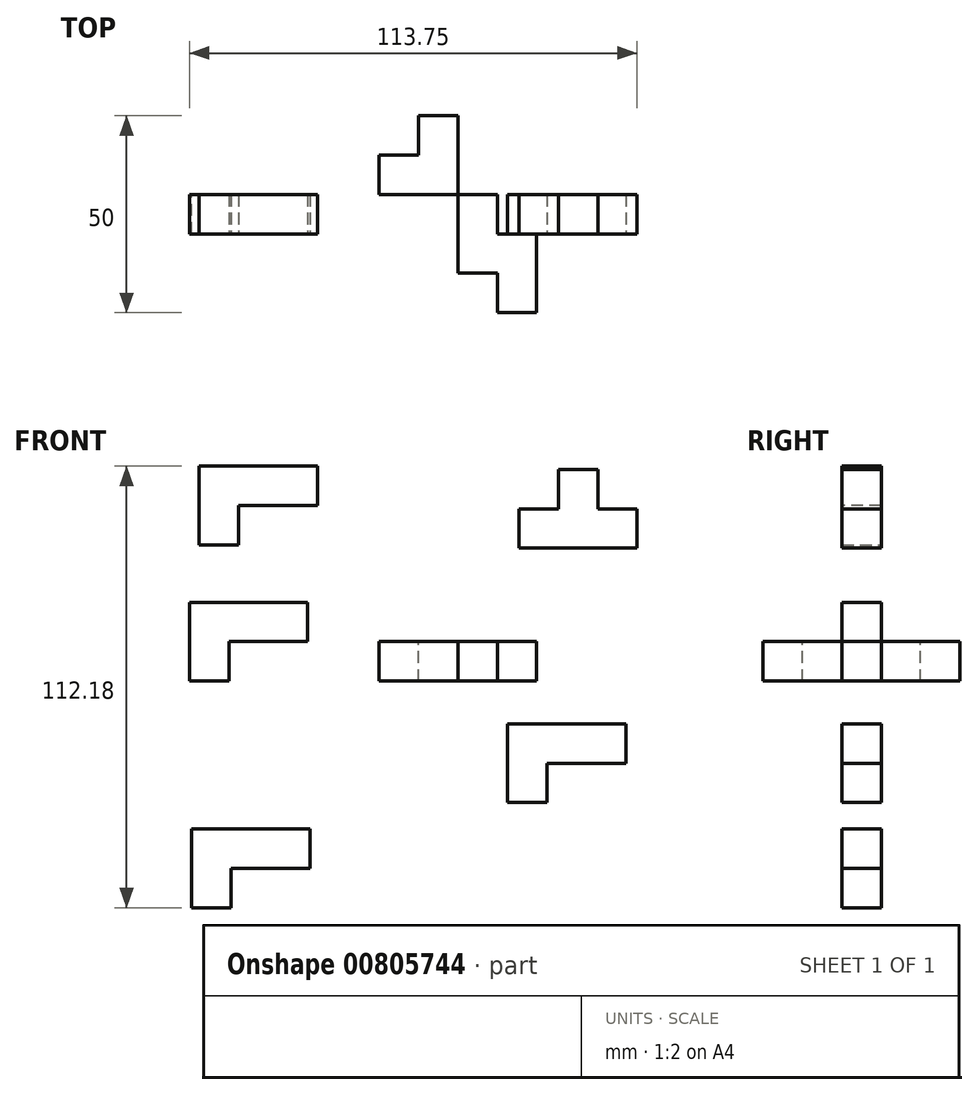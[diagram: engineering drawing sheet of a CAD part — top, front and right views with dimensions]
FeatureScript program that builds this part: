
annotation { "Feature Type Name" : "Feature", "Feature Type Description" : "" }
export const myFeature = defineFeature(function(context is Context, id is Id, definition is map)
    precondition{}
    {
        {
            var Q0;
            Q0=qCreatedBy(makeId("Top.planeOp"),FACE);
            var sketch = newSketch(context, id + "F0", { "sketchPlane" : qUnion([Q0])});
            skLineSegment(sketch, "E0.bottom", {"start": v(0, 0) * mm, "end": v(20, 0) * mm});
            skLineSegment(sketch, "E0.top", {"start": v(0, -30) * mm, "end": v(20, -30) * mm});
            skLineSegment(sketch, "E0.left", {"start": v(0, 0) * mm, "end": v(0, -30) * mm});
            skLineSegment(sketch, "E0.right", {"start": v(20, 0) * mm, "end": v(20, -30) * mm});
            skSolve(sketch);
        }
        {
            var Q0;
            Q0 = qSketchRegion(id + "F0", true);
            extrude(context, id + "F1", {"entities" : qUnion([Q0]), "depth" : 10 * mm, "offsetDistance" : 25 * mm});
        }
        {
            var Q0;
            Q0=makeQuery(id+"F1.opExtrude","CAP_FACE",FACE,{"disambiguationData":[OSD([sQuery(id+"F0.wireOp",EDGE,"E0.bottom"),sQuery(id+"F0.wireOp",EDGE,"E0.top"),sQuery(id+"F0.wireOp",EDGE,"E0.left"),sQuery(id+"F0.wireOp",EDGE,"E0.right")])],"isStart":false});
            var sketch = newSketch(context, id + "F2", { "sketchPlane" : qUnion([Q0])});
            skLineSegment(sketch, "E1.bottom", {"start": v(20, 0) * mm, "end": v(10, 0) * mm});
            skLineSegment(sketch, "E1.top", {"start": v(20, -10) * mm, "end": v(10, -10) * mm});
            skLineSegment(sketch, "E1.left", {"start": v(20, 0) * mm, "end": v(20, -10) * mm});
            skLineSegment(sketch, "E1.right", {"start": v(10, 0) * mm, "end": v(10, -10) * mm});
            skLineSegment(sketch, "E2.bottom", {"start": v(0, -30) * mm, "end": v(10, -30) * mm});
            skLineSegment(sketch, "E2.top", {"start": v(0, -20) * mm, "end": v(10, -20) * mm});
            skLineSegment(sketch, "E2.left", {"start": v(0, -30) * mm, "end": v(0, -20) * mm});
            skLineSegment(sketch, "E2.right", {"start": v(10, -30) * mm, "end": v(10, -20) * mm});
            skSolve(sketch);
        }
        {
            var Q0;
            Q0=qCreatedBy(makeId("Top.planeOp"),FACE);
            var sketch = newSketch(context, id + "F3", { "sketchPlane" : qUnion([Q0])});
            skLineSegment(sketch, "E3.bottom", {"start": v(0, 0) * mm, "end": v(-20, 0) * mm});
            skLineSegment(sketch, "E3.top", {"start": v(0, 20) * mm, "end": v(-20, 20) * mm});
            skLineSegment(sketch, "E3.left", {"start": v(0, 0) * mm, "end": v(0, 20) * mm});
            skLineSegment(sketch, "E3.right", {"start": v(-20, 0) * mm, "end": v(-20, 20) * mm});
            skSolve(sketch);
        }
        {
            var Q0;
            Q0=makeQuery(id+"F3.imprint","IMPRINT",FACE,{"disambiguationData":[TD([[makeQuery(id+"F3.imprint","IMPRINT",EDGE,{"derivedFrom":sQuery(id+"F3.wireOp",EDGE,"E3.bottom")}),-1.0]])]});
            extrude(context, id + "F4", {"entities" : qUnion([Q0]), "depth" : 10 * mm, "offsetDistance" : 25 * mm});
        }
        {
            var Q0;
            Q0=makeQuery(id+"F4.opExtrude","CAP_FACE",FACE,{"disambiguationData":[OSD([sQuery(id+"F3.wireOp",EDGE,"E3.bottom"),sQuery(id+"F3.wireOp",EDGE,"E3.top"),sQuery(id+"F3.wireOp",EDGE,"E3.left"),sQuery(id+"F3.wireOp",EDGE,"E3.right")])],"isStart":false});
            var sketch = newSketch(context, id + "F5", { "sketchPlane" : qUnion([Q0])});
            skSolve(sketch);
        }
        {
            var Q0;
            Q0=makeQuery(id+"F5.imprint","IMPRINT",FACE,{"disambiguationData":[TD([[makeQuery(id+"F5.imprint","IMPRINT",EDGE,{"derivedFrom":makeQuery(id+"F4.opExtrude","CAP_EDGE",EDGE,{"disambiguationData":[OSD([sQuery(id+"F3.wireOp",EDGE,"E3.bottom")])],"isStart":false})}),-1.0]])]});
            var sketch = newSketch(context, id + "F6", { "sketchPlane" : qUnion([Q0])});
            skLineSegment(sketch, "E4.bottom", {"start": v(-20, 20) * mm, "end": v(-10, 20) * mm});
            skLineSegment(sketch, "E4.top", {"start": v(-20, 10) * mm, "end": v(-10, 10) * mm});
            skLineSegment(sketch, "E4.left", {"start": v(-20, 20) * mm, "end": v(-20, 10) * mm});
            skLineSegment(sketch, "E4.right", {"start": v(-10, 20) * mm, "end": v(-10, 10) * mm});
            skSolve(sketch);
        }
        {
            var Q0;
            Q0=makeQuery(id+"F6.imprint","IMPRINT",FACE,{"disambiguationData":[TD([[makeQuery(id+"F6.imprint","IMPRINT",EDGE,{"derivedFrom":sQuery(id+"F6.wireOp",EDGE,"E4.bottom")}),1.0]])]});
            extrude(context, id + "F7", {"entities" : qUnion([Q0]), "operationType" : NewBodyOperationType.REMOVE, "oppositeDirection" : true, "depth" : 10 * mm, "offsetDistance" : 25 * mm});
        }
        {
            var Q0;
            Q0=makeQuery(id+"F2.imprint","IMPRINT",FACE,{"disambiguationData":[TD([[makeQuery(id+"F2.imprint","IMPRINT",EDGE,{"derivedFrom":sQuery(id+"F2.wireOp",EDGE,"E1.bottom")}),-1.0]])]});
            var Q1;
            Q1=makeQuery(id+"F2.imprint","IMPRINT",FACE,{"disambiguationData":[TD([[makeQuery(id+"F2.imprint","IMPRINT",EDGE,{"derivedFrom":sQuery(id+"F2.wireOp",EDGE,"E2.bottom")}),1.0]])]});
            extrude(context, id + "F8", {"entities" : qUnion([Q0, Q1]), "operationType" : NewBodyOperationType.REMOVE, "oppositeDirection" : true, "depth" : 10 * mm, "offsetDistance" : 25 * mm});
        }
        {
            var Q0;
            Q0=qCreatedBy(makeId("Front.planeOp"),FACE);
            var sketch = newSketch(context, id + "F9", { "sketchPlane" : qUnion([Q0])});
            skLineSegment(sketch, "E5.bottom", {"start": v(-68.2, 0) * mm, "end": v(-38.2, 0) * mm});
            skLineSegment(sketch, "E5.top", {"start": v(-68.2, 20) * mm, "end": v(-38.2, 20) * mm});
            skLineSegment(sketch, "E5.left", {"start": v(-68.2, 0) * mm, "end": v(-68.2, 20) * mm});
            skLineSegment(sketch, "E5.right", {"start": v(-38.2, 0) * mm, "end": v(-38.2, 20) * mm});
            skSolve(sketch);
        }
        {
            var Q0;
            Q0=makeQuery(id+"F9.imprint","IMPRINT",FACE,{"disambiguationData":[TD([[makeQuery(id+"F9.imprint","IMPRINT",EDGE,{"derivedFrom":sQuery(id+"F9.wireOp",EDGE,"E5.bottom")}),1.0]])]});
            extrude(context, id + "F10", {"entities" : qUnion([Q0]), "depth" : 10 * mm, "offsetDistance" : 25 * mm});
        }
        {
            var Q0;
            Q0=makeQuery(id+"F10.opExtrude","CAP_FACE",FACE,{"disambiguationData":[OSD([sQuery(id+"F9.wireOp",EDGE,"E5.bottom"),sQuery(id+"F9.wireOp",EDGE,"E5.top"),sQuery(id+"F9.wireOp",EDGE,"E5.left"),sQuery(id+"F9.wireOp",EDGE,"E5.right")])],"isStart":false});
            var sketch = newSketch(context, id + "F11", { "sketchPlane" : qUnion([Q0])});
            skLineSegment(sketch, "E6.bottom", {"start": v(-38.2, 0) * mm, "end": v(-58.2, 0) * mm});
            skLineSegment(sketch, "E6.top", {"start": v(-38.2, 10) * mm, "end": v(-58.2, 10) * mm});
            skLineSegment(sketch, "E6.left", {"start": v(-38.2, 0) * mm, "end": v(-38.2, 10) * mm});
            skLineSegment(sketch, "E6.right", {"start": v(-58.2, 0) * mm, "end": v(-58.2, 10) * mm});
            skSolve(sketch);
        }
        {
            var Q0;
            Q0=makeQuery(id+"F11.imprint","IMPRINT",FACE,{"disambiguationData":[TD([[makeQuery(id+"F11.imprint","IMPRINT",EDGE,{"derivedFrom":sQuery(id+"F11.wireOp",EDGE,"E6.bottom")}),1.0]])]});
            extrude(context, id + "F12", {"entities" : qUnion([Q0]), "operationType" : NewBodyOperationType.REMOVE, "oppositeDirection" : true, "depth" : 10 * mm, "offsetDistance" : 25 * mm});
        }
        {
            var Q0;
            Q0=qCreatedBy(makeId("Front.planeOp"),FACE);
            var sketch = newSketch(context, id + "F13", { "sketchPlane" : qUnion([Q0])});
            skLineSegment(sketch, "E7.bottom", {"start": v(-67.63, -57.59) * mm, "end": v(-37.63, -57.59) * mm});
            skLineSegment(sketch, "E7.top", {"start": v(-67.63, -37.59) * mm, "end": v(-37.63, -37.59) * mm});
            skLineSegment(sketch, "E7.left", {"start": v(-67.63, -57.59) * mm, "end": v(-67.63, -37.59) * mm});
            skLineSegment(sketch, "E7.right", {"start": v(-37.63, -57.59) * mm, "end": v(-37.63, -37.59) * mm});
            skSolve(sketch);
        }
        {
            var Q0;
            Q0=makeQuery(id+"F13.imprint","IMPRINT",FACE,{"disambiguationData":[TD([[makeQuery(id+"F13.imprint","IMPRINT",EDGE,{"derivedFrom":sQuery(id+"F13.wireOp",EDGE,"E7.bottom")}),1.0]])]});
            extrude(context, id + "F14", {"entities" : qUnion([Q0]), "depth" : 10 * mm, "offsetDistance" : 25 * mm});
        }
        {
            var Q0;
            Q0=makeQuery(id+"F14.opExtrude","CAP_FACE",FACE,{"disambiguationData":[OSD([sQuery(id+"F13.wireOp",EDGE,"E7.bottom"),sQuery(id+"F13.wireOp",EDGE,"E7.top"),sQuery(id+"F13.wireOp",EDGE,"E7.left"),sQuery(id+"F13.wireOp",EDGE,"E7.right")])],"isStart":false});
            var sketch = newSketch(context, id + "F15", { "sketchPlane" : qUnion([Q0])});
            skLineSegment(sketch, "E8.bottom", {"start": v(-37.63, -57.59) * mm, "end": v(-57.63, -57.59) * mm});
            skLineSegment(sketch, "E8.top", {"start": v(-37.63, -47.59) * mm, "end": v(-57.63, -47.59) * mm});
            skLineSegment(sketch, "E8.left", {"start": v(-37.63, -57.59) * mm, "end": v(-37.63, -47.59) * mm});
            skLineSegment(sketch, "E8.right", {"start": v(-57.63, -57.59) * mm, "end": v(-57.63, -47.59) * mm});
            skSolve(sketch);
        }
        {
            var Q0;
            Q0=makeQuery(id+"F15.imprint","IMPRINT",FACE,{"disambiguationData":[TD([[makeQuery(id+"F15.imprint","IMPRINT",EDGE,{"derivedFrom":sQuery(id+"F15.wireOp",EDGE,"E8.bottom")}),1.0]])]});
            extrude(context, id + "F16", {"entities" : qUnion([Q0]), "operationType" : NewBodyOperationType.REMOVE, "oppositeDirection" : true, "depth" : 10 * mm, "offsetDistance" : 25 * mm});
        }
        {
            var Q0;
            Q0=qCreatedBy(makeId("Front.planeOp"),FACE);
            var sketch = newSketch(context, id + "F17", { "sketchPlane" : qUnion([Q0])});
            skLineSegment(sketch, "E9.bottom", {"start": v(15.54, 33.74) * mm, "end": v(45.54, 33.74) * mm});
            skLineSegment(sketch, "E9.top", {"start": v(15.54, 53.74) * mm, "end": v(45.54, 53.74) * mm});
            skLineSegment(sketch, "E9.left", {"start": v(15.54, 33.74) * mm, "end": v(15.54, 53.74) * mm});
            skLineSegment(sketch, "E9.right", {"start": v(45.54, 33.74) * mm, "end": v(45.54, 53.74) * mm});
            skSolve(sketch);
        }
        {
            var Q0;
            Q0=makeQuery(id+"F17.imprint","IMPRINT",FACE,{"disambiguationData":[TD([[makeQuery(id+"F17.imprint","IMPRINT",EDGE,{"derivedFrom":sQuery(id+"F17.wireOp",EDGE,"E9.bottom")}),1.0]])]});
            extrude(context, id + "F18", {"entities" : qUnion([Q0]), "depth" : 10 * mm, "offsetDistance" : 25 * mm});
        }
        {
            var Q0;
            Q0=makeQuery(id+"F18.opExtrude","CAP_FACE",FACE,{"disambiguationData":[OSD([sQuery(id+"F17.wireOp",EDGE,"E9.bottom"),sQuery(id+"F17.wireOp",EDGE,"E9.top"),sQuery(id+"F17.wireOp",EDGE,"E9.left"),sQuery(id+"F17.wireOp",EDGE,"E9.right")])],"isStart":false});
            var sketch = newSketch(context, id + "F19", { "sketchPlane" : qUnion([Q0])});
            skLineSegment(sketch, "E10.bottom", {"start": v(15.54, 53.74) * mm, "end": v(25.54, 53.74) * mm});
            skLineSegment(sketch, "E10.top", {"start": v(15.54, 43.74) * mm, "end": v(25.54, 43.74) * mm});
            skLineSegment(sketch, "E10.left", {"start": v(15.54, 53.74) * mm, "end": v(15.54, 43.74) * mm});
            skLineSegment(sketch, "E10.right", {"start": v(25.54, 53.74) * mm, "end": v(25.54, 43.74) * mm});
            skLineSegment(sketch, "E11.bottom", {"start": v(45.54, 53.74) * mm, "end": v(35.54, 53.74) * mm});
            skLineSegment(sketch, "E11.top", {"start": v(45.54, 43.74) * mm, "end": v(35.54, 43.74) * mm});
            skLineSegment(sketch, "E11.left", {"start": v(45.54, 53.74) * mm, "end": v(45.54, 43.74) * mm});
            skLineSegment(sketch, "E11.right", {"start": v(35.54, 53.74) * mm, "end": v(35.54, 43.74) * mm});
            skSolve(sketch);
        }
        {
            var Q0;
            Q0=makeQuery(id+"F19.imprint","IMPRINT",FACE,{"disambiguationData":[TD([[makeQuery(id+"F19.imprint","IMPRINT",EDGE,{"derivedFrom":sQuery(id+"F19.wireOp",EDGE,"E10.bottom")}),-1.0]])]});
            var Q1;
            Q1=makeQuery(id+"F19.imprint","IMPRINT",FACE,{"disambiguationData":[TD([[makeQuery(id+"F19.imprint","IMPRINT",EDGE,{"derivedFrom":sQuery(id+"F19.wireOp",EDGE,"E11.bottom")}),-1.0]])]});
            extrude(context, id + "F20", {"entities" : qUnion([Q0, Q1]), "operationType" : NewBodyOperationType.REMOVE, "oppositeDirection" : true, "depth" : 10 * mm, "offsetDistance" : 25 * mm});
        }
        {
            var Q0;
            Q0=qCreatedBy(makeId("Front.planeOp"),FACE);
            var sketch = newSketch(context, id + "F21", { "sketchPlane" : qUnion([Q0])});
            skLineSegment(sketch, "E12.bottom", {"start": v(-65.73, 34.6) * mm, "end": v(-35.73, 34.6) * mm});
            skLineSegment(sketch, "E12.top", {"start": v(-65.73, 54.6) * mm, "end": v(-35.73, 54.6) * mm});
            skLineSegment(sketch, "E12.left", {"start": v(-65.73, 34.6) * mm, "end": v(-65.73, 54.6) * mm});
            skLineSegment(sketch, "E12.right", {"start": v(-35.73, 34.6) * mm, "end": v(-35.73, 54.6) * mm});
            skSolve(sketch);
        }
        {
            var Q0;
            Q0 = qSketchRegion(id + "F21", true);
            extrude(context, id + "F22", {"entities" : qUnion([Q0]), "depth" : 10 * mm, "offsetDistance" : 25 * mm});
        }
        {
            var Q0;
            Q0=qCreatedBy(makeId("Front.planeOp"),FACE);
            var sketch = newSketch(context, id + "F23", { "sketchPlane" : qUnion([Q0])});
            skLineSegment(sketch, "E13.bottom", {"start": v(12.64, -30.9) * mm, "end": v(42.64, -30.9) * mm});
            skLineSegment(sketch, "E13.top", {"start": v(12.64, -10.9) * mm, "end": v(42.64, -10.9) * mm});
            skLineSegment(sketch, "E13.left", {"start": v(12.64, -30.9) * mm, "end": v(12.64, -10.9) * mm});
            skLineSegment(sketch, "E13.right", {"start": v(42.64, -30.9) * mm, "end": v(42.64, -10.9) * mm});
            skSolve(sketch);
        }
        {
            var Q0;
            Q0 = qSketchRegion(id + "F23", true);
            extrude(context, id + "F24", {"entities" : qUnion([Q0]), "depth" : 10 * mm, "offsetDistance" : 25 * mm});
        }
        {
            var Q0;
            Q0=makeQuery(id+"F22.opExtrude","CAP_FACE",FACE,{"disambiguationData":[OSD([sQuery(id+"F21.wireOp",EDGE,"E12.bottom"),sQuery(id+"F21.wireOp",EDGE,"E12.top"),sQuery(id+"F21.wireOp",EDGE,"E12.left"),sQuery(id+"F21.wireOp",EDGE,"E12.right")])],"isStart":false});
            var sketch = newSketch(context, id + "F25", { "sketchPlane" : qUnion([Q0])});
            skLineSegment(sketch, "E14.bottom", {"start": v(-35.73, 34.6) * mm, "end": v(-55.73, 34.6) * mm});
            skLineSegment(sketch, "E14.top", {"start": v(-35.73, 44.6) * mm, "end": v(-55.73, 44.6) * mm});
            skLineSegment(sketch, "E14.left", {"start": v(-35.73, 34.6) * mm, "end": v(-35.73, 44.6) * mm});
            skLineSegment(sketch, "E14.right", {"start": v(-55.73, 34.6) * mm, "end": v(-55.73, 44.6) * mm});
            skSolve(sketch);
        }
        {
            var Q0;
            Q0=makeQuery(id+"F25.imprint","IMPRINT",FACE,{"disambiguationData":[TD([[makeQuery(id+"F25.imprint","IMPRINT",EDGE,{"derivedFrom":sQuery(id+"F25.wireOp",EDGE,"E14.bottom")}),1.0]])]});
            extrude(context, id + "F26", {"entities" : qUnion([Q0]), "operationType" : NewBodyOperationType.REMOVE, "oppositeDirection" : true, "depth" : 10 * mm, "offsetDistance" : 25 * mm});
        }
        {
            var Q0;
            Q0=makeQuery(id+"F24.opExtrude","CAP_FACE",FACE,{"disambiguationData":[OSD([sQuery(id+"F23.wireOp",EDGE,"E13.bottom"),sQuery(id+"F23.wireOp",EDGE,"E13.top"),sQuery(id+"F23.wireOp",EDGE,"E13.left"),sQuery(id+"F23.wireOp",EDGE,"E13.right")])],"isStart":false});
            var sketch = newSketch(context, id + "F27", { "sketchPlane" : qUnion([Q0])});
            skLineSegment(sketch, "E15.bottom", {"start": v(42.64, -30.9) * mm, "end": v(22.64, -30.9) * mm});
            skLineSegment(sketch, "E15.top", {"start": v(42.64, -20.9) * mm, "end": v(22.64, -20.9) * mm});
            skLineSegment(sketch, "E15.left", {"start": v(42.64, -30.9) * mm, "end": v(42.64, -20.9) * mm});
            skLineSegment(sketch, "E15.right", {"start": v(22.64, -30.9) * mm, "end": v(22.64, -20.9) * mm});
            skSolve(sketch);
        }
        {
            var Q0;
            Q0=makeQuery(id+"F27.imprint","IMPRINT",FACE,{"disambiguationData":[TD([[makeQuery(id+"F27.imprint","IMPRINT",EDGE,{"derivedFrom":sQuery(id+"F27.wireOp",EDGE,"E15.bottom")}),1.0]])]});
            extrude(context, id + "F28", {"entities" : qUnion([Q0]), "operationType" : NewBodyOperationType.REMOVE, "oppositeDirection" : true, "depth" : 10 * mm, "offsetDistance" : 25 * mm});
        }
    });
